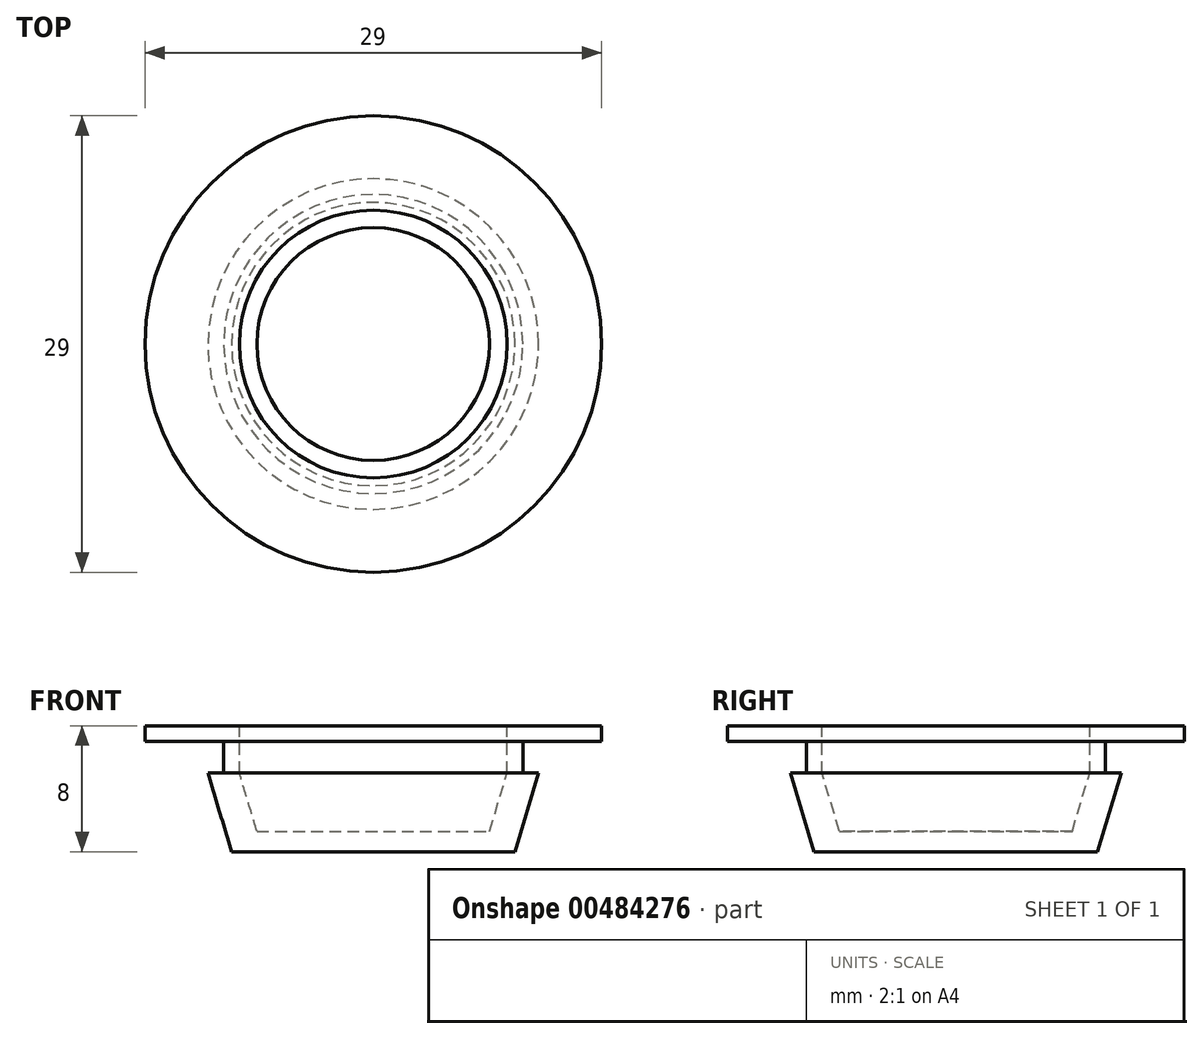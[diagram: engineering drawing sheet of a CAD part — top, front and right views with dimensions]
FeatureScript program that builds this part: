
annotation { "Feature Type Name" : "Feature", "Feature Type Description" : "" }
export const myFeature = defineFeature(function(context is Context, id is Id, definition is map)
    precondition{}
    {
        {
            var Q0;
            Q0=qCreatedBy(makeId("Front.planeOp"),FACE);
            var sketch = newSketch(context, id + "F0", { "sketchPlane" : qUnion([Q0])});
            skLineSegment(sketch, "E0", {"start": v(0, 0) * mm, "end": v(-9, 0) * mm});
            skLineSegment(sketch, "E1", {"start": v(0, 0) * mm, "end": v(0, 1.3) * mm});
            skLineSegment(sketch, "E2", {"start": v(0, 1.3) * mm, "end": v(-9, 1.3) * mm});
            skLineSegment(sketch, "E3", {"start": v(-9, 1.3) * mm, "end": v(-9, 0) * mm});
            skLineSegment(sketch, "E4", {"start": v(-9, 0) * mm, "end": v(-10.5, 5) * mm});
            skLineSegment(sketch, "E5", {"start": v(-10.5, 5) * mm, "end": v(-8.5, 5) * mm});
            skLineSegment(sketch, "E6", {"start": v(-9, 0) * mm, "end": v(-7, 0) * mm});
            skLineSegment(sketch, "E7", {"start": v(-7, 0) * mm, "end": v(-8.5, 5) * mm});
            skLineSegment(sketch, "E8", {"start": v(-10.5, 5) * mm, "end": v(-9.5, 5) * mm});
            skLineSegment(sketch, "E9", {"start": v(-9.5, 5) * mm, "end": v(-9.5, 7) * mm});
            skLineSegment(sketch, "E10", {"start": v(-9.5, 8) * mm, "end": v(-9.5, 7) * mm});
            skLineSegment(sketch, "E11", {"start": v(-8.5, 5) * mm, "end": v(-8.5, 7) * mm});
            skLineSegment(sketch, "E12", {"start": v(-9.5, 7) * mm, "end": v(-8.5, 7) * mm});
            skLineSegment(sketch, "E13", {"start": v(-8.5, 7) * mm, "end": v(-8.5, 8) * mm});
            skLineSegment(sketch, "E14", {"start": v(-8.5, 8) * mm, "end": v(-14.5, 8) * mm});
            skLineSegment(sketch, "E15", {"start": v(-14.5, 8) * mm, "end": v(-14.5, 7) * mm});
            skLineSegment(sketch, "E16", {"start": v(-14.5, 7) * mm, "end": v(-8.5, 7) * mm});
            skSolve(sketch);
        }
        {
            var Q0;
            {var subQ0=sQuery(id+"F0.wireOp",EDGE,"E0");Q0=makeQuery(id+"F0.imprint","IMPRINT",FACE,{"disambiguationData":[TD([[makeQuery(id+"F0.imprint","IMPRINT",EDGE,{"derivedFrom":subQ0}),-1.0]])]});}
            var Q1;
            {var subQ0=sQuery(id+"F0.wireOp",EDGE,"E3");Q1=makeQuery(id+"F0.imprint","IMPRINT",FACE,{"disambiguationData":[TD([[makeQuery(id+"F0.imprint","IMPRINT",EDGE,{"derivedFrom":subQ0}),1.0]])]});}
            var Q2;
            {var subQ1=sQuery(id+"F0.wireOp",EDGE,"E3");Q2=makeQuery(id+"F0.imprint","IMPRINT",FACE,{"disambiguationData":[TD([[makeQuery(id+"F0.imprint","IMPRINT",EDGE,{"derivedFrom":subQ1}),-1.0]])]});}
            var Q3;
            Q3=makeQuery(id+"F0.imprint","IMPRINT",FACE,{"disambiguationData":[TD([[makeQuery(id+"F0.imprint","IMPRINT",EDGE,{"derivedFrom":sQuery(id+"F0.wireOp",EDGE,"E5")}),1.0]])]});
            var Q4;
            {var subQ0=sQuery(id+"F0.wireOp",EDGE,"E10");Q4=makeQuery(id+"F0.imprint","IMPRINT",FACE,{"disambiguationData":[TD([[makeQuery(id+"F0.imprint","IMPRINT",EDGE,{"derivedFrom":subQ0}),1.0]])]});}
            var Q5;
            {var subQ0=sQuery(id+"F0.wireOp",EDGE,"E10");Q5=makeQuery(id+"F0.imprint","IMPRINT",FACE,{"disambiguationData":[TD([[makeQuery(id+"F0.imprint","IMPRINT",EDGE,{"derivedFrom":subQ0}),-1.0]])]});}
            var Q6;
            Q6=sQuery(id+"F0.wireOp",EDGE,"E1");
            revolve(context, id + "F1", {"entities" : qUnion([Q0, Q1, Q2, Q3, Q4, Q5]), "axis" : qUnion([Q6]), "revolveType" : RevolveType.FULL});
        }
    });
